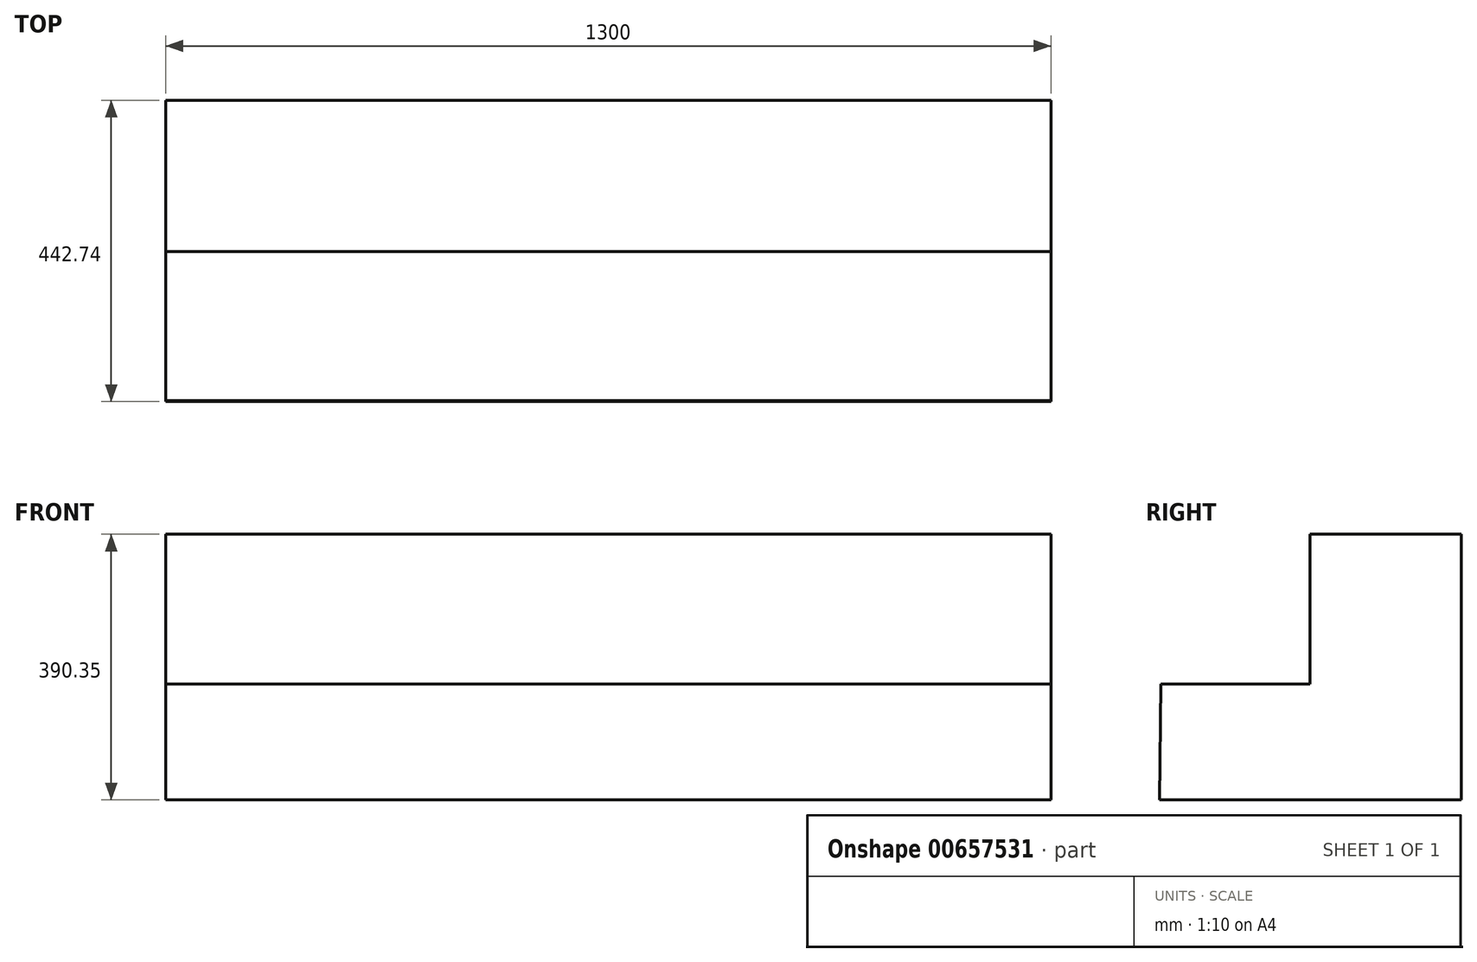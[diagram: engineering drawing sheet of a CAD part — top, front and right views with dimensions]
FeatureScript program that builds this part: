
annotation { "Feature Type Name" : "Feature", "Feature Type Description" : "" }
export const myFeature = defineFeature(function(context is Context, id is Id, definition is map)
    precondition{}
    {
        {
            var Q0;
            Q0=qCreatedBy(makeId("Right.planeOp"),FACE);
            var sketch = newSketch(context, id + "F0", { "sketchPlane" : qUnion([Q0])});
            skLineSegment(sketch, "E0", {"start": v(-23.83, -25.16) * mm, "end": v(418.9, -25.16) * mm});
            skLineSegment(sketch, "E1", {"start": v(418.9, -25.16) * mm, "end": v(418.9, 365.19) * mm});
            skLineSegment(sketch, "E2", {"start": v(418.9, 365.19) * mm, "end": v(196.6, 365.19) * mm});
            skLineSegment(sketch, "E3", {"start": v(196.6, 365.19) * mm, "end": v(196.6, 145.3) * mm});
            skLineSegment(sketch, "E4", {"start": v(196.6, 145.3) * mm, "end": v(-22.3, 145.3) * mm});
            skLineSegment(sketch, "E5", {"start": v(-22.3, 145.3) * mm, "end": v(-23.83, -25.16) * mm});
            skSolve(sketch);
        }
        {
            var Q0;
            Q0=makeQuery(id+"F0.imprint","IMPRINT",FACE,{"disambiguationData":[TD([[makeQuery(id+"F0.imprint","IMPRINT",EDGE,{"derivedFrom":sQuery(id+"F0.wireOp",EDGE,"E0")}),1.0]])]});
            extrude(context, id + "F1", {"entities" : qUnion([Q0]), "depth" : 1300 * mm, "offsetDistance" : 25 * mm});
        }
    });
